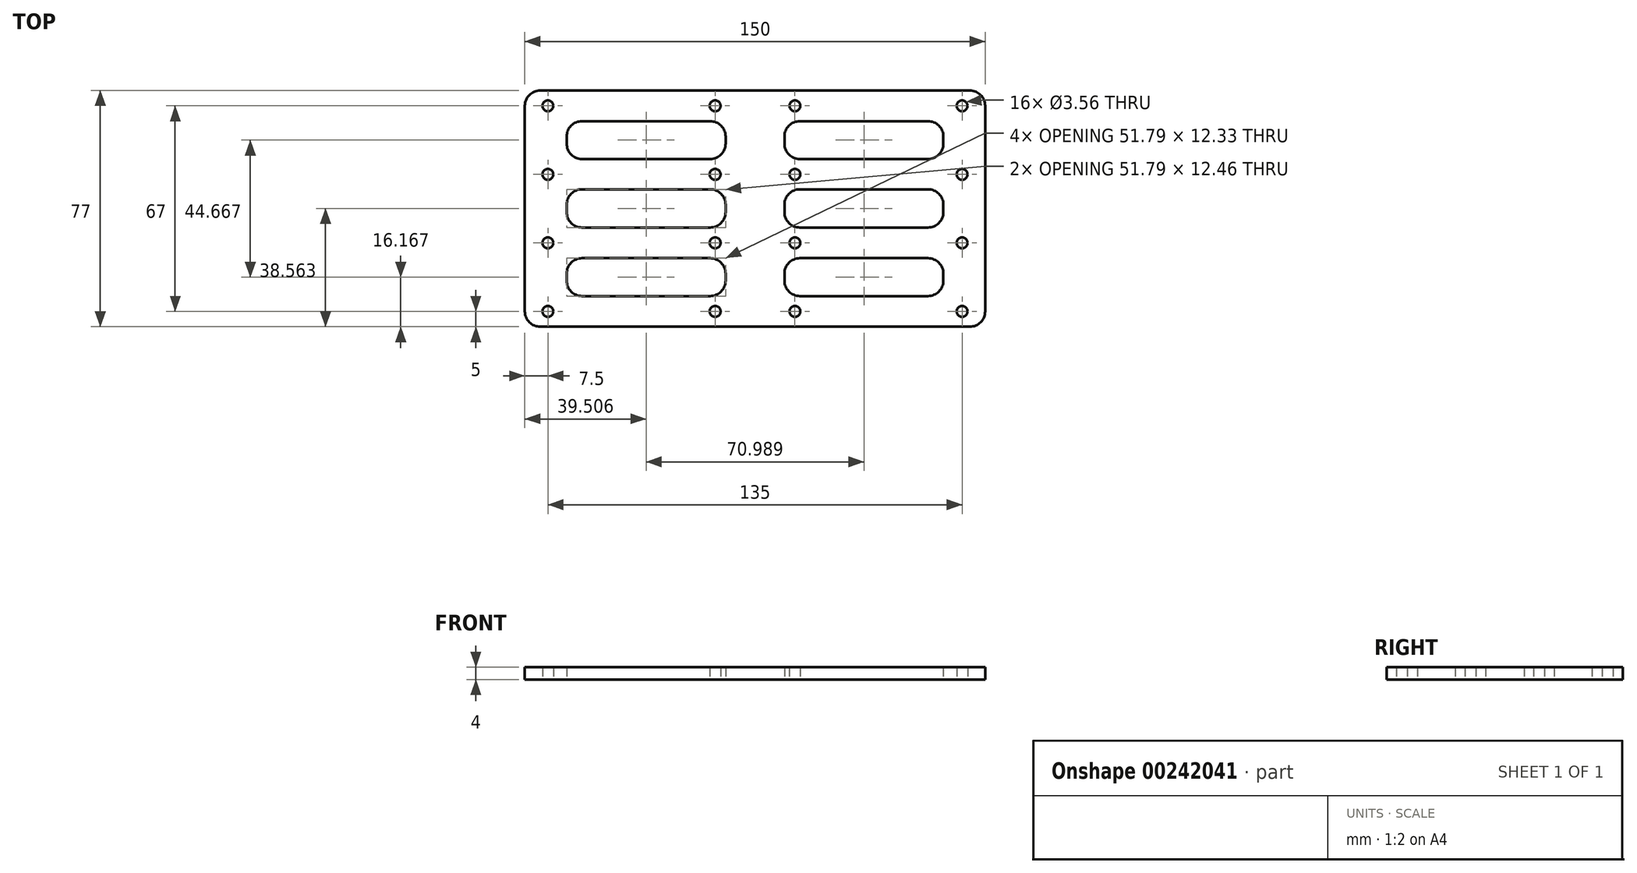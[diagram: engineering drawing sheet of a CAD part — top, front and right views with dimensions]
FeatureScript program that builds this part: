
annotation { "Feature Type Name" : "Feature", "Feature Type Description" : "" }
export const myFeature = defineFeature(function(context is Context, id is Id, definition is map)
    precondition{}
    {
        {
            var Q0;
            Q0=qCreatedBy(makeId("Top.planeOp"),FACE);
            var sketch = newSketch(context, id + "F0", { "sketchPlane" : qUnion([Q0])});
            skLineSegment(sketch, "E0.bottom", {"start": v(5, 0) * mm, "end": v(75, 0) * mm});
            skLineSegment(sketch, "E0.top", {"start": v(18.61, 10) * mm, "end": v(60.4, 10) * mm});
            skLineSegment(sketch, "E0.left", {"start": v(0, 5) * mm, "end": v(0, 10) * mm});
            skCircle(sketch, "E1", {"center": v(7.5, 5) * mm, "radius": 1.78 * mm});
            skPoint(sketch, "E2", {"position": v(0, 5) * mm});
            skCircle(sketch, "E3.1.0.0", {"center": v(62, 5) * mm, "radius": 1.78 * mm});
            skLineSegment(sketch, "E3.direction1", {"start": v(7.5, 5) * mm, "end": v(62, 5) * mm, "construction": true});
            skLineSegment(sketch, "E4", {"start": v(75, 10) * mm, "end": v(75, 0) * mm, "construction": true});
            skLineSegment(sketch, "E5.0.1.0", {"start": v(18.61, 32.33) * mm, "end": v(60.4, 32.33) * mm});
            skLineSegment(sketch, "E5.0.1.1", {"start": v(18.61, 22.33) * mm, "end": v(60.4, 22.33) * mm});
            skPoint(sketch, "E5.0.1.2", {"position": v(0, 27.33) * mm});
            skLineSegment(sketch, "E5.0.1.5", {"start": v(75, 32.33) * mm, "end": v(75, 22.33) * mm, "construction": true});
            skLineSegment(sketch, "E5.0.1.6", {"start": v(7.5, 27.33) * mm, "end": v(62, 27.33) * mm, "construction": true});
            skCircle(sketch, "E5.0.1.7", {"center": v(62, 27.33) * mm, "radius": 1.78 * mm});
            skCircle(sketch, "E5.0.1.8", {"center": v(7.5, 27.33) * mm, "radius": 1.78 * mm});
            skLineSegment(sketch, "E5.0.1.10", {"start": v(0, 22.33) * mm, "end": v(0, 32.33) * mm});
            skLineSegment(sketch, "E5.direction1", {"start": v(0, 0) * mm, "end": v(25, 0) * mm, "construction": true});
            skLineSegment(sketch, "E5.direction2", {"start": v(0, 0) * mm, "end": v(0, 22.33) * mm, "construction": true});
            skLineSegment(sketch, "E6", {"start": v(0, 32.33) * mm, "end": v(0, 44.8) * mm, "construction": true});
            skLineSegment(sketch, "E7", {"start": v(18.61, 44.8) * mm, "end": v(65.4, 44.8) * mm, "construction": true});
            skLineSegment(sketch, "E8.0.0.2", {"start": v(18.61, 54.67) * mm, "end": v(60.4, 54.67) * mm});
            skPoint(sketch, "E8.6.0.2", {"position": v(0, 49.67) * mm});
            skLineSegment(sketch, "E8.11.0.2", {"start": v(75, 54.67) * mm, "end": v(75, 44.67) * mm, "construction": true});
            skLineSegment(sketch, "E8.14.0.2", {"start": v(7.5, 49.67) * mm, "end": v(62, 49.67) * mm, "construction": true});
            skCircle(sketch, "E8.17.0.2", {"center": v(62, 49.67) * mm, "radius": 1.78 * mm});
            skCircle(sketch, "E8.19.0.2", {"center": v(7.5, 49.67) * mm, "radius": 1.78 * mm});
            skLineSegment(sketch, "E8.24.0.2", {"start": v(0, 44.67) * mm, "end": v(0, 54.67) * mm});
            skLineSegment(sketch, "E8.0.0.3", {"start": v(5, 77) * mm, "end": v(75, 77) * mm});
            skPoint(sketch, "E8.6.0.3", {"position": v(0, 72) * mm});
            skLineSegment(sketch, "E8.11.0.3", {"start": v(75, 77) * mm, "end": v(75, 67) * mm, "construction": true});
            skLineSegment(sketch, "E8.14.0.3", {"start": v(7.5, 72) * mm, "end": v(62, 72) * mm, "construction": true});
            skCircle(sketch, "E8.17.0.3", {"center": v(62, 72) * mm, "radius": 1.78 * mm});
            skCircle(sketch, "E8.19.0.3", {"center": v(7.5, 72) * mm, "radius": 1.78 * mm});
            skLineSegment(sketch, "E8.24.0.3", {"start": v(0, 67) * mm, "end": v(0, 72) * mm});
            skLineSegment(sketch, "E9", {"start": v(0, 67) * mm, "end": v(0, 54.67) * mm});
            skLineSegment(sketch, "E10", {"start": v(0, 44.8) * mm, "end": v(0, 32.33) * mm});
            skLineSegment(sketch, "E11", {"start": v(0, 22.33) * mm, "end": v(0, 10) * mm});
            skLineSegment(sketch, "E12", {"start": v(13.61, 62) * mm, "end": v(13.61, 59.67) * mm});
            skLineSegment(sketch, "E13.trimOffspring", {"start": v(13.61, 39.8) * mm, "end": v(13.61, 37.33) * mm});
            skLineSegment(sketch, "E14.trimOffspring", {"start": v(13.61, 17.33) * mm, "end": v(13.61, 15) * mm});
            skLineSegment(sketch, "E15", {"start": v(18.61, 67) * mm, "end": v(60.4, 67) * mm});
            skPoint(sketch, "E16.visualSharp", {"position": v(0, 77) * mm});
            skArc(sketch, "E16.filletArc", {"start": v(5, 77) * mm, "mid": v(1.46, 75.54) * mm, "end": v(0, 72) * mm});
            skPoint(sketch, "E17.visualSharp", {"position": v(13.61, 67) * mm});
            skArc(sketch, "E17.filletArc", {"start": v(18.61, 67) * mm, "mid": v(15.08, 65.54) * mm, "end": v(13.61, 62) * mm});
            skPoint(sketch, "E18.visualSharp", {"position": v(13.61, 54.67) * mm});
            skArc(sketch, "E18.filletArc", {"start": v(13.61, 59.67) * mm, "mid": v(15.08, 56.13) * mm, "end": v(18.61, 54.67) * mm});
            skPoint(sketch, "E19.visualSharp", {"position": v(0, 0) * mm});
            skArc(sketch, "E19.filletArc", {"start": v(0, 5) * mm, "mid": v(1.46, 1.46) * mm, "end": v(5, 0) * mm});
            skPoint(sketch, "E20.visualSharp", {"position": v(13.61, 10) * mm});
            skArc(sketch, "E20.filletArc", {"start": v(13.61, 15) * mm, "mid": v(15.08, 11.46) * mm, "end": v(18.61, 10) * mm});
            skPoint(sketch, "E21.visualSharp", {"position": v(13.61, 22.33) * mm});
            skArc(sketch, "E21.filletArc", {"start": v(18.61, 22.33) * mm, "mid": v(15.08, 20.87) * mm, "end": v(13.61, 17.33) * mm});
            skPoint(sketch, "E22.visualSharp", {"position": v(13.61, 32.33) * mm});
            skArc(sketch, "E22.filletArc", {"start": v(13.61, 37.33) * mm, "mid": v(15.08, 33.8) * mm, "end": v(18.61, 32.33) * mm});
            skPoint(sketch, "E23.visualSharp", {"position": v(13.61, 44.8) * mm});
            skArc(sketch, "E23.filletArc", {"start": v(18.61, 44.8) * mm, "mid": v(15.08, 43.33) * mm, "end": v(13.61, 39.8) * mm});
            skLineSegment(sketch, "E24", {"start": v(65.4, 62) * mm, "end": v(65.4, 59.67) * mm});
            skLineSegment(sketch, "E25.trimOffspring", {"start": v(65.4, 39.8) * mm, "end": v(65.4, 37.33) * mm});
            skLineSegment(sketch, "E26.trimOffspring", {"start": v(65.4, 17.33) * mm, "end": v(65.4, 15) * mm});
            skLineSegment(sketch, "E27.MirrorCS", {"start": v(150, 5) * mm, "end": v(150, 10) * mm});
            skLineSegment(sketch, "E28.MirrorCS", {"start": v(136.39, 62) * mm, "end": v(136.39, 59.67) * mm});
            skArc(sketch, "E29.MirrorCS", {"start": v(150, 5) * mm, "mid": v(148.54, 1.46) * mm, "end": v(145, 0) * mm});
            skArc(sketch, "E30.MirrorCS", {"start": v(131.39, 44.8) * mm, "mid": v(134.92, 43.33) * mm, "end": v(136.39, 39.8) * mm});
            skLineSegment(sketch, "E31.MirrorCS", {"start": v(150, 67) * mm, "end": v(150, 72) * mm});
            skLineSegment(sketch, "E32.MirrorCS", {"start": v(136.39, 17.33) * mm, "end": v(136.39, 15) * mm});
            skLineSegment(sketch, "E33.MirrorCS", {"start": v(136.39, 39.8) * mm, "end": v(136.39, 37.33) * mm});
            skLineSegment(sketch, "E34.MirrorCS", {"start": v(150, 44.8) * mm, "end": v(150, 32.33) * mm});
            skArc(sketch, "E35.MirrorCS", {"start": v(136.39, 15) * mm, "mid": v(134.92, 11.46) * mm, "end": v(131.39, 10) * mm});
            skLineSegment(sketch, "E36.MirrorCS", {"start": v(150, 44.67) * mm, "end": v(150, 54.67) * mm});
            skArc(sketch, "E37.MirrorCS", {"start": v(136.39, 37.33) * mm, "mid": v(134.92, 33.8) * mm, "end": v(131.39, 32.33) * mm});
            skArc(sketch, "E38.MirrorCS", {"start": v(136.39, 59.67) * mm, "mid": v(134.92, 56.13) * mm, "end": v(131.39, 54.67) * mm});
            skArc(sketch, "E39.MirrorCS", {"start": v(145, 77) * mm, "mid": v(148.54, 75.54) * mm, "end": v(150, 72) * mm});
            skArc(sketch, "E40.MirrorCS", {"start": v(131.39, 67) * mm, "mid": v(134.92, 65.54) * mm, "end": v(136.39, 62) * mm});
            skLineSegment(sketch, "E41.MirrorCS", {"start": v(150, 22.33) * mm, "end": v(150, 32.33) * mm});
            skLineSegment(sketch, "E42.MirrorCS", {"start": v(150, 22.33) * mm, "end": v(150, 10) * mm});
            skArc(sketch, "E43.MirrorCS", {"start": v(131.39, 22.33) * mm, "mid": v(134.92, 20.87) * mm, "end": v(136.39, 17.33) * mm});
            skLineSegment(sketch, "E44.MirrorCS", {"start": v(145, 0) * mm, "end": v(75, 0) * mm});
            skLineSegment(sketch, "E45.MirrorCS", {"start": v(131.39, 54.67) * mm, "end": v(89.6, 54.67) * mm});
            skLineSegment(sketch, "E46.MirrorCS", {"start": v(84.6, 17.33) * mm, "end": v(84.6, 15) * mm});
            skCircle(sketch, "E47.MirrorC", {"center": v(88, 72) * mm, "radius": 1.78 * mm});
            skPoint(sketch, "E48.MirrorP", {"position": v(150, 72) * mm});
            skLineSegment(sketch, "E49.MirrorCS", {"start": v(150, 0) * mm, "end": v(150, 22.33) * mm, "construction": true});
            skLineSegment(sketch, "E50.MirrorCS", {"start": v(131.39, 32.33) * mm, "end": v(89.6, 32.33) * mm});
            skLineSegment(sketch, "E51.MirrorCS", {"start": v(131.39, 10) * mm, "end": v(89.6, 10) * mm});
            skLineSegment(sketch, "E52.MirrorCS", {"start": v(131.39, 22.33) * mm, "end": v(89.6, 22.33) * mm});
            skPoint(sketch, "E53.MirrorP", {"position": v(150, 5) * mm});
            skPoint(sketch, "E54.MirrorP", {"position": v(136.39, 32.33) * mm});
            skPoint(sketch, "E55.MirrorP", {"position": v(136.39, 67) * mm});
            skLineSegment(sketch, "E56.MirrorCS", {"start": v(131.39, 44.8) * mm, "end": v(89.6, 44.8) * mm, "construction": true});
            skPoint(sketch, "E57.MirrorP", {"position": v(150, 77) * mm});
            skLineSegment(sketch, "E58.MirrorCS", {"start": v(142.5, 49.67) * mm, "end": v(88, 49.67) * mm, "construction": true});
            skPoint(sketch, "E59.MirrorP", {"position": v(136.39, 44.8) * mm});
            skLineSegment(sketch, "E60.MirrorCS", {"start": v(84.6, 62) * mm, "end": v(84.6, 59.67) * mm});
            skLineSegment(sketch, "E61.MirrorCS", {"start": v(131.39, 67) * mm, "end": v(89.6, 67) * mm});
            skPoint(sketch, "E62.MirrorP", {"position": v(136.39, 22.33) * mm});
            skCircle(sketch, "E63.MirrorC", {"center": v(88, 5) * mm, "radius": 1.78 * mm});
            skLineSegment(sketch, "E64.MirrorCS", {"start": v(142.5, 5) * mm, "end": v(88, 5) * mm, "construction": true});
            skLineSegment(sketch, "E65.MirrorCS", {"start": v(142.5, 27.33) * mm, "end": v(88, 27.33) * mm, "construction": true});
            skCircle(sketch, "E66.MirrorC", {"center": v(142.5, 27.33) * mm, "radius": 1.78 * mm});
            skCircle(sketch, "E67.MirrorC", {"center": v(88, 49.67) * mm, "radius": 1.78 * mm});
            skLineSegment(sketch, "E68.MirrorCS", {"start": v(150, 67) * mm, "end": v(150, 54.67) * mm});
            skLineSegment(sketch, "E69.MirrorCS", {"start": v(145, 77) * mm, "end": v(75, 77) * mm});
            skPoint(sketch, "E70.MirrorP", {"position": v(150, 27.33) * mm});
            skCircle(sketch, "E71.MirrorC", {"center": v(142.5, 72) * mm, "radius": 1.78 * mm});
            skLineSegment(sketch, "E72.MirrorCS", {"start": v(150, 32.33) * mm, "end": v(150, 44.8) * mm, "construction": true});
            skCircle(sketch, "E73.MirrorC", {"center": v(142.5, 49.67) * mm, "radius": 1.78 * mm});
            skPoint(sketch, "E74.MirrorP", {"position": v(136.39, 54.67) * mm});
            skPoint(sketch, "E75.MirrorP", {"position": v(136.39, 10) * mm});
            skLineSegment(sketch, "E76.MirrorCS", {"start": v(142.5, 72) * mm, "end": v(88, 72) * mm, "construction": true});
            skLineSegment(sketch, "E77.MirrorCS", {"start": v(150, 0) * mm, "end": v(125, 0) * mm, "construction": true});
            skLineSegment(sketch, "E78.MirrorCS", {"start": v(84.6, 39.8) * mm, "end": v(84.6, 37.33) * mm});
            skPoint(sketch, "E79.MirrorP", {"position": v(150, 0) * mm});
            skCircle(sketch, "E80.MirrorC", {"center": v(88, 27.33) * mm, "radius": 1.78 * mm});
            skPoint(sketch, "E81.MirrorP", {"position": v(150, 49.67) * mm});
            skCircle(sketch, "E82.MirrorC", {"center": v(142.5, 5) * mm, "radius": 1.78 * mm});
            skPoint(sketch, "E83.visualSharp", {"position": v(65.4, 10) * mm});
            skArc(sketch, "E83.filletArc", {"start": v(60.4, 10) * mm, "mid": v(63.94, 11.46) * mm, "end": v(65.4, 15) * mm});
            skPoint(sketch, "E84.visualSharp", {"position": v(65.4, 22.33) * mm});
            skArc(sketch, "E84.filletArc", {"start": v(65.4, 17.33) * mm, "mid": v(63.94, 20.87) * mm, "end": v(60.4, 22.33) * mm});
            skPoint(sketch, "E85.visualSharp", {"position": v(84.6, 22.33) * mm});
            skArc(sketch, "E85.filletArc", {"start": v(89.6, 22.33) * mm, "mid": v(86.06, 20.87) * mm, "end": v(84.6, 17.33) * mm});
            skPoint(sketch, "E86.visualSharp", {"position": v(84.6, 10) * mm});
            skArc(sketch, "E86.filletArc", {"start": v(84.6, 15) * mm, "mid": v(86.06, 11.46) * mm, "end": v(89.6, 10) * mm});
            skPoint(sketch, "E87.visualSharp", {"position": v(65.4, 32.33) * mm});
            skArc(sketch, "E87.filletArc", {"start": v(60.4, 32.33) * mm, "mid": v(63.94, 33.8) * mm, "end": v(65.4, 37.33) * mm});
            skPoint(sketch, "E88.visualSharp", {"position": v(84.6, 32.33) * mm});
            skArc(sketch, "E88.filletArc", {"start": v(84.6, 37.33) * mm, "mid": v(86.06, 33.8) * mm, "end": v(89.6, 32.33) * mm});
            skPoint(sketch, "E89.visualSharp", {"position": v(84.6, 44.8) * mm});
            skArc(sketch, "E89.filletArc", {"start": v(89.6, 44.8) * mm, "mid": v(86.06, 43.33) * mm, "end": v(84.6, 39.8) * mm});
            skPoint(sketch, "E90.visualSharp", {"position": v(65.4, 67) * mm});
            skArc(sketch, "E90.filletArc", {"start": v(65.4, 62) * mm, "mid": v(63.94, 65.54) * mm, "end": v(60.4, 67) * mm});
            skPoint(sketch, "E91.visualSharp", {"position": v(84.6, 67) * mm});
            skArc(sketch, "E91.filletArc", {"start": v(89.6, 67) * mm, "mid": v(86.06, 65.54) * mm, "end": v(84.6, 62) * mm});
            skPoint(sketch, "E92.visualSharp", {"position": v(84.6, 54.67) * mm});
            skArc(sketch, "E92.filletArc", {"start": v(84.6, 59.67) * mm, "mid": v(86.06, 56.13) * mm, "end": v(89.6, 54.67) * mm});
            skPoint(sketch, "E93.visualSharp", {"position": v(65.4, 54.67) * mm});
            skArc(sketch, "E93.filletArc", {"start": v(60.4, 54.67) * mm, "mid": v(63.94, 56.13) * mm, "end": v(65.4, 59.67) * mm});
            skLineSegment(sketch, "E94", {"start": v(18.61, 44.8) * mm, "end": v(60.4, 44.8) * mm});
            skLineSegment(sketch, "E95", {"start": v(89.6, 44.8) * mm, "end": v(131.39, 44.8) * mm});
            skPoint(sketch, "E96.visualSharp", {"position": v(65.4, 44.8) * mm});
            skArc(sketch, "E96.filletArc", {"start": v(65.4, 39.8) * mm, "mid": v(63.94, 43.33) * mm, "end": v(60.4, 44.8) * mm});
            skSolve(sketch);
        }
        {
            var Q0;
            Q0=qSketchRegion(id+"F0",true);
            extrude(context, id + "F1", {"entities" : qUnion([Q0]), "depth" : 3.5 * mm});
        }
        {
            var Q0;
            Q0 = qSketchRegion(id + "F0", true);
            extrude(context, id + "F2", {"entities" : qUnion([Q0]), "operationType" : NewBodyOperationType.ADD, "depth" : 4 * mm});
        }
    });
